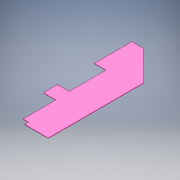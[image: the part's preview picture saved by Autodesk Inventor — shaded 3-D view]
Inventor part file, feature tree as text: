
AUTODESK INVENTOR PART (.ipt)
format: ipt  version: 2018 (Build 220112000, 112)  size: 121,856 bytes
history: native  units: mm
features: extrude x1, sketch x1
ambient origin geometry x8: Origin, YZ Plane, XZ Plane, XY Plane, X Axis, Y Axis, Z Axis, Center Point
bodies: Solid1 (feature_tree)
feature tree (2):
  extrude  "Extrusion1"  Depth=75.0mm
  sketch  "Sketch1"  dims[d0=240.0mm d1=75.0mm d4=235.0mm d5=75.0mm d6=90.0mm d7=80.0mm d8=210.0mm d9=35.0mm d10=25.0mm d12=1.6mm d13=0.0mm d16=75.0mm d17=270.0mm d18=45.0deg]
